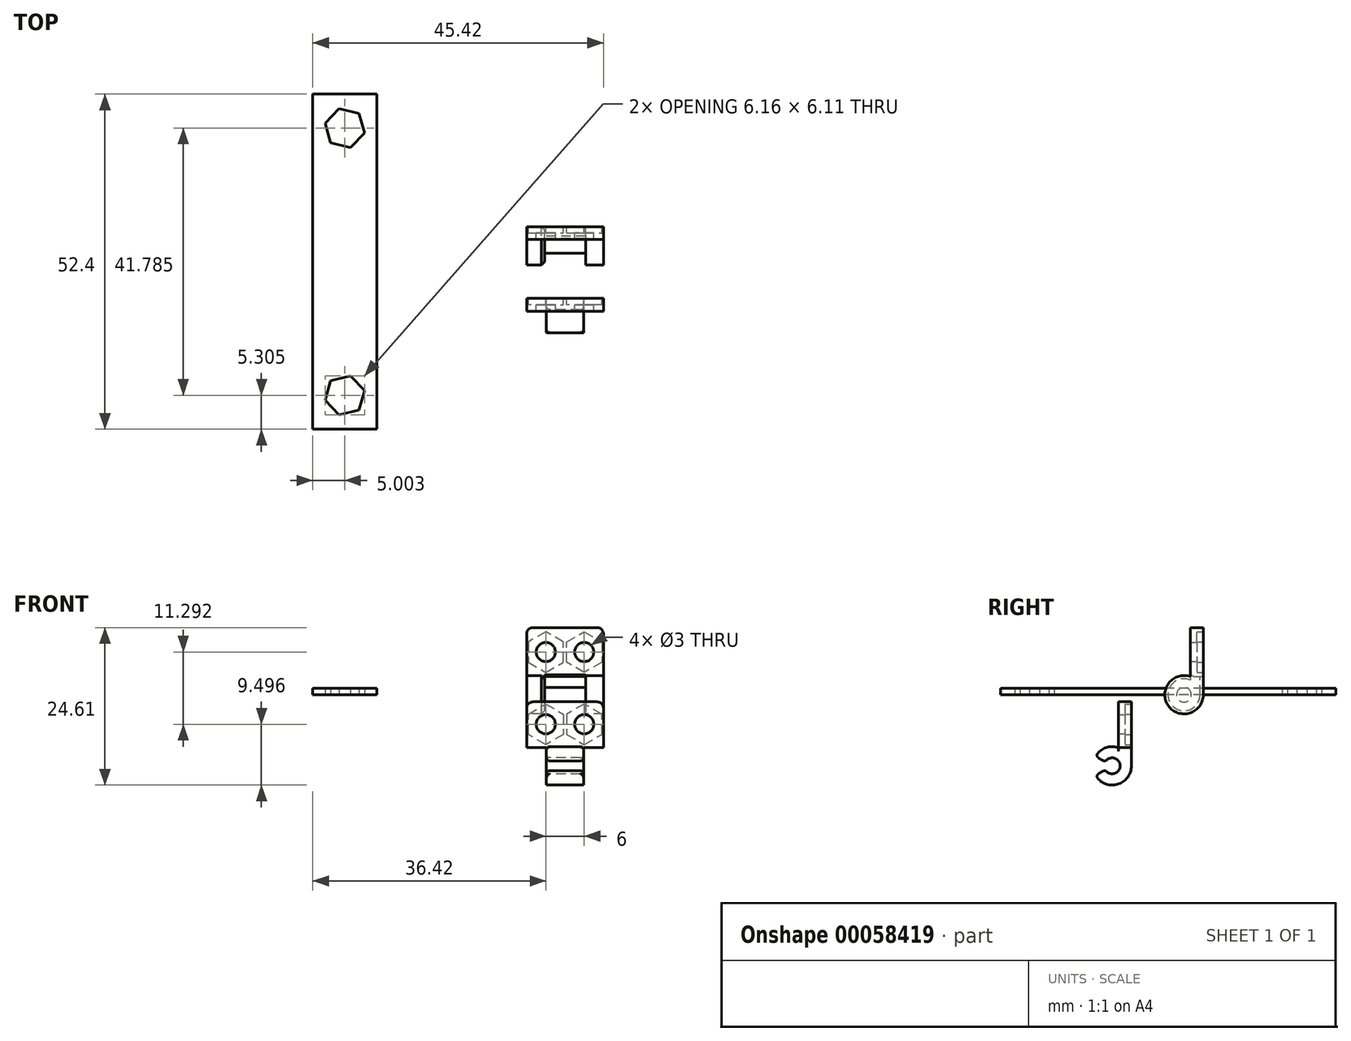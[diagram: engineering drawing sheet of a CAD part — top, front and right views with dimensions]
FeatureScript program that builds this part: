
annotation { "Feature Type Name" : "Feature", "Feature Type Description" : "" }
export const myFeature = defineFeature(function(context is Context, id is Id, definition is map)
    precondition{}
    {
        {
            var Q0;
            Q0=qCreatedBy(makeId("Right.planeOp"),FACE);
            var sketch = newSketch(context, id + "F0", { "sketchPlane" : qUnion([Q0])});
            skCircle(sketch, "E0", {"center": v(-1, 0) * mm, "radius": 3 * mm});
            skLineSegment(sketch, "E1", {"start": v(2, 0) * mm, "end": v(2, 10.5) * mm});
            skLineSegment(sketch, "E2", {"start": v(2, 10.5) * mm, "end": v(0, 10.5) * mm});
            skLineSegment(sketch, "E3", {"start": v(0, 10.5) * mm, "end": v(0, 2.83) * mm});
            skCircle(sketch, "E4", {"center": v(-1, 0) * mm, "radius": 1.15 * mm});
            skLineSegment(sketch, "E5", {"start": v(0, 2.83) * mm, "end": v(2, 2.83) * mm});
            skLineSegment(sketch, "E6", {"start": v(-1, 0) * mm, "end": v(2, 0) * mm, "construction": true});
            skSolve(sketch);
        }
        {
            var Q0;
            Q0=qSketchRegion(id+"F0",true);
            var Q1;
            Q1=makeQuery(id+"F0.imprint","IMPRINT",FACE,{"disambiguationData":[TD([[makeQuery(id+"F0.imprint","IMPRINT",EDGE,{"derivedFrom":sQuery(id+"F0.wireOp",EDGE,"E4")}),1.0]])]});
            var Q2;
            Q2=qBodyType(qCreatedBy(id+"FAZ1pR2O8vTgytI_1",FACE),BodyType.SOLID);
            extrude(context, id + "F1", {"entities" : qUnion([Q0, Q1]), "endBoundEntityFace" : qUnion([Q2]), "depth" : 6 * mm, "hasSecondDirection" : true, "secondDirectionOppositeDirection" : true, "secondDirectionDepth" : 6 * mm});
        }
        {
            var Q0;
            Q0=makeQuery(id+"F0.imprint","IMPRINT",FACE,{"disambiguationData":[TD([[makeQuery(id+"F0.imprint","IMPRINT",EDGE,{"derivedFrom":sQuery(id+"F0.wireOp",EDGE,"E4")}),-1.0]])]});
            var Q1;
            {var subQ0=sQuery(id+"F0.wireOp",EDGE,"E5");Q1=makeQuery(id+"F0.imprint","IMPRINT",FACE,{"disambiguationData":[TD([[makeQuery(id+"F0.imprint","IMPRINT",EDGE,{"derivedFrom":subQ0}),-1.0]])]});}
            extrude(context, id + "F2", {"entities" : qUnion([Q0, Q1]), "operationType" : NewBodyOperationType.REMOVE, "depth" : 3.2 * mm, "hasSecondDirection" : true, "secondDirectionOppositeDirection" : true, "secondDirectionDepth" : 3.2 * mm});
        }
        {
            var Q0;
            Q0=makeQuery(id+"F1.opExtrude","SWEPT_FACE",FACE,{"disambiguationData":[OSD([sQuery(id+"F0.wireOp",EDGE,"E1")])]});
            var sketch = newSketch(context, id + "F3", { "sketchPlane" : qUnion([Q0])});
            skLineSegment(sketch, "E7", {"start": v(-6, 6.68) * mm, "end": v(6, 6.68) * mm, "construction": true});
            skLineSegment(sketch, "E8", {"start": v(0, 10.5) * mm, "end": v(0, 2.83) * mm, "construction": true});
            skCircle(sketch, "E9.cCircle", {"center": v(3, 6.68) * mm, "radius": 2.75 * mm, "construction": true});
            skLineSegment(sketch, "E9.0", {"start": v(3, 3.5) * mm, "end": v(0.25, 5.1) * mm});
            skLineSegment(sketch, "E9.1", {"start": v(0.25, 5.1) * mm, "end": v(0.25, 8.27) * mm});
            skLineSegment(sketch, "E9.2", {"start": v(0.25, 8.27) * mm, "end": v(3, 9.85) * mm});
            skLineSegment(sketch, "E9.3", {"start": v(3, 9.85) * mm, "end": v(5.75, 8.27) * mm});
            skLineSegment(sketch, "E9.4", {"start": v(5.75, 8.27) * mm, "end": v(5.75, 5.1) * mm});
            skLineSegment(sketch, "E9.5", {"start": v(5.75, 5.1) * mm, "end": v(3, 3.5) * mm});
            skPoint(sketch, "E9.0.midPoint", {"position": v(1.63, 4.3) * mm});
            skLineSegment(sketch, "E10", {"start": v(3, 9.85) * mm, "end": v(3, 3.5) * mm, "construction": true});
            skLineSegment(sketch, "E11.MirrorCS", {"start": v(-3, 9.85) * mm, "end": v(-5.75, 8.27) * mm});
            skLineSegment(sketch, "E12.MirrorCS", {"start": v(-0.25, 8.27) * mm, "end": v(-3, 9.85) * mm});
            skLineSegment(sketch, "E13.MirrorCS", {"start": v(-0.25, 5.1) * mm, "end": v(-0.25, 8.27) * mm});
            skLineSegment(sketch, "E14.MirrorCS", {"start": v(-3, 3.5) * mm, "end": v(-0.25, 5.1) * mm});
            skLineSegment(sketch, "E15.MirrorCS", {"start": v(-5.75, 5.1) * mm, "end": v(-3, 3.5) * mm});
            skLineSegment(sketch, "E16.MirrorCS", {"start": v(-5.75, 8.27) * mm, "end": v(-5.75, 5.1) * mm});
            skLineSegment(sketch, "E17", {"start": v(-3, 9.85) * mm, "end": v(-3, 3.5) * mm, "construction": true});
            skPoint(sketch, "E18", {"position": v(-3, 6.68) * mm});
            skSolve(sketch);
        }
        {
            var Q0;
            Q0=makeQuery(id+"F3.imprint","IMPRINT",FACE,{"disambiguationData":[TD([[makeQuery(id+"F3.imprint","IMPRINT",EDGE,{"derivedFrom":sQuery(id+"F3.wireOp",EDGE,"E9.0")}),-1.0]])]});
            var Q1;
            Q1=makeQuery(id+"F3.imprint","IMPRINT",FACE,{"disambiguationData":[TD([[makeQuery(id+"F3.imprint","IMPRINT",EDGE,{"derivedFrom":sQuery(id+"F3.wireOp",EDGE,"E11.MirrorCS")}),1.0]])]});
            var Q2;
            {var subQ9=sQuery(id+"F3.wireOp",EDGE,"E9.1");Q2=makeQuery(id+"F3.imprint","IMPRINT",FACE,{"disambiguationData":[TD([[makeQuery(id+"F3.imprint","IMPRINT",EDGE,{"derivedFrom":subQ9}),-1.0]])]});}
            extrude(context, id + "F4", {"entities" : qUnion([Q0, Q1, Q2]), "operationType" : NewBodyOperationType.REMOVE, "oppositeDirection" : true, "depth" : 1 * mm});
        }
        {
            var Q0;
            Q0=sQuery(id+"F3.wireOp",VERTEX,"E9.cCircle.center");
            var Q1;
            Q1=sQuery(id+"F3.wireOp",VERTEX,"E18");
            var Q2;
            Q2=makeQuery(id+"F1.opExtrude","SWEPT_BODY",BODY,{"disambiguationData":[OSD([sQuery(id+"F0.wireOp",EDGE,"E0"),sQuery(id+"F0.wireOp",EDGE,"E1"),sQuery(id+"F0.wireOp",EDGE,"E2"),sQuery(id+"F0.wireOp",EDGE,"E3")])]});
            hole(context, id + "F5", {"style" : HoleStyle.SIMPLE, "holeDiameter" : 3 * mm, "endStyle" : HoleEndStyle.THROUGH, "locations" : qUnion([Q0, Q1]), "scope" : qUnion([Q2])});
        }
        {
            var Q0;
            Q0=qCreatedBy(makeId("Right.planeOp"),FACE);
            var sketch = newSketch(context, id + "F6", { "sketchPlane" : qUnion([Q0])});
            skCircle(sketch, "E19", {"center": v(-12.22, -11.11) * mm, "radius": 3 * mm});
            skLineSegment(sketch, "E20", {"start": v(-9.22, -11.11) * mm, "end": v(-9.22, -1.11) * mm});
            skLineSegment(sketch, "E21", {"start": v(-9.22, -1.11) * mm, "end": v(-11.22, -1.11) * mm});
            skLineSegment(sketch, "E22", {"start": v(-11.22, -1.11) * mm, "end": v(-11.22, -8.29) * mm});
            skLineSegment(sketch, "E23", {"start": v(-9.22, -11.11) * mm, "end": v(-12.22, -11.11) * mm, "construction": true});
            skCircle(sketch, "E24", {"center": v(-12.22, -11.11) * mm, "radius": 1.25 * mm});
            skLineSegment(sketch, "E25", {"start": v(-12.22, -11.11) * mm, "end": v(-14.82, -9.61) * mm});
            skLineSegment(sketch, "E26", {"start": v(-12.22, -11.11) * mm, "end": v(-14.82, -12.61) * mm});
            skLineSegment(sketch, "E27", {"start": v(-11.22, -8.29) * mm, "end": v(-9.22, -8.29) * mm});
            skSolve(sketch);
        }
        {
            var Q0;
            {var subQ1=sQuery(id+"F6.wireOp",EDGE,"E20");Q0=makeQuery(id+"F6.imprint","IMPRINT",FACE,{"disambiguationData":[TD([[makeQuery(id+"F6.imprint","IMPRINT",EDGE,{"derivedFrom":subQ1}),1.0]])]});}
            var Q1;
            {var subQ3=sQuery(id+"F6.wireOp",EDGE,"E19");var subQ9=makeQuery(id+"F6.imprint","INTERSECT",VERTEX,{"derivedFrom":[subQ3,sQuery(id+"F6.wireOp",EDGE,"E20")]});Q1=makeQuery(id+"F6.imprint","IMPRINT",FACE,{"disambiguationData":[TD([[makeQuery(id+"F6.imprint","IMPRINT",EDGE,{"disambiguationData":[TD([[subQ9,-1.0]])],"derivedFrom":subQ3}),1.0]])]});}
            extrude(context, id + "F7", {"entities" : qUnion([Q0, Q1]), "depth" : 2.9 * mm, "hasSecondDirection" : true, "secondDirectionOppositeDirection" : true, "secondDirectionDepth" : 2.9 * mm});
        }
        {
            var Q0;
            {var subQ1=sQuery(id+"F6.wireOp",EDGE,"E21");Q0=makeQuery(id+"F6.imprint","IMPRINT",FACE,{"disambiguationData":[TD([[makeQuery(id+"F6.imprint","IMPRINT",EDGE,{"derivedFrom":subQ1}),1.0]])]});}
            extrude(context, id + "F8", {"entities" : qUnion([Q0]), "operationType" : NewBodyOperationType.ADD, "endBound" : BoundingType.SYMMETRIC, "depth" : 12 * mm});
        }
        {
            var Q0;
            Q0=makeQuery(id+"F7.opExtrude","SWEPT_EDGE",EDGE,{"disambiguationData":[OSD([sQuery(id+"F6.wireOp",EDGE,"E24"),sQuery(id+"F6.wireOp",EDGE,"E25")])]});
            var Q1;
            Q1=makeQuery(id+"F7.opExtrude","SWEPT_EDGE",EDGE,{"disambiguationData":[OSD([sQuery(id+"F6.wireOp",EDGE,"E24"),sQuery(id+"F6.wireOp",EDGE,"E26")])]});
            var Q2;
            Q2=makeQuery(id+"F7.opExtrude","CAP_EDGE",EDGE,{"disambiguationData":[OSD([sQuery(id+"F6.wireOp",EDGE,"E24")])],"isStart":false});
            var Q3;
            Q3=makeQuery(id+"F7.opExtrude","CAP_EDGE",EDGE,{"disambiguationData":[OSD([sQuery(id+"F6.wireOp",EDGE,"E24")])],"isStart":true});
            var Q4;
            Q4=makeQuery(id+"F7.opExtrude","SWEPT_EDGE",EDGE,{"disambiguationData":[OSD([sQuery(id+"F6.wireOp",EDGE,"E19"),sQuery(id+"F6.wireOp",EDGE,"E25")])]});
            var Q5;
            Q5=makeQuery(id+"F7.opExtrude","CAP_EDGE",EDGE,{"disambiguationData":[OSD([sQuery(id+"F6.wireOp",EDGE,"E26")])],"isStart":false});
            var Q6;
            Q6=makeQuery(id+"F7.opExtrude","SWEPT_EDGE",EDGE,{"disambiguationData":[OSD([sQuery(id+"F6.wireOp",EDGE,"E19"),sQuery(id+"F6.wireOp",EDGE,"E26")])]});
            var Q7;
            Q7=makeQuery(id+"F7.opExtrude","CAP_EDGE",EDGE,{"disambiguationData":[OSD([sQuery(id+"F6.wireOp",EDGE,"E25")])],"isStart":false});
            var Q8;
            Q8=makeQuery(id+"F7.opExtrude","CAP_EDGE",EDGE,{"disambiguationData":[OSD([sQuery(id+"F6.wireOp",EDGE,"E25")])],"isStart":true});
            var Q9;
            Q9=makeQuery(id+"F7.opExtrude","CAP_EDGE",EDGE,{"disambiguationData":[OSD([sQuery(id+"F6.wireOp",EDGE,"E26")])],"isStart":true});
            var Q10;
            {var subQ0=sQuery(id+"F6.wireOp",EDGE,"E19");Q10=makeQuery(id+"F7.opExtrude","CAP_EDGE",EDGE,{"disambiguationData":[OSD([subQ0]),TDD([makeQuery(id+"F6.imprint","IMPRINT",EDGE,{"disambiguationData":[TD([[makeQuery(id+"F6.imprint","INTERSECT",VERTEX,{"derivedFrom":[subQ0,sQuery(id+"F6.wireOp",EDGE,"E22")]}),-1.0]])],"derivedFrom":subQ0})])],"isStart":false});}
            var Q11;
            {var subQ0=sQuery(id+"F6.wireOp",EDGE,"E19");Q11=makeQuery(id+"F7.opExtrude","CAP_EDGE",EDGE,{"disambiguationData":[OSD([subQ0]),TDD([makeQuery(id+"F6.imprint","IMPRINT",EDGE,{"disambiguationData":[TD([[makeQuery(id+"F6.imprint","INTERSECT",VERTEX,{"derivedFrom":[subQ0,sQuery(id+"F6.wireOp",EDGE,"E22")]}),-1.0]])],"derivedFrom":subQ0})])],"isStart":true});}
            var Q12;
            Q12=makeQuery(id+"F7.opExtrude","CAP_EDGE",EDGE,{"disambiguationData":[OSD([sQuery(id+"F6.wireOp",EDGE,"E21")])],"isStart":false});
            var Q13;
            Q13=makeQuery(id+"F7.opExtrude","CAP_EDGE",EDGE,{"disambiguationData":[OSD([sQuery(id+"F6.wireOp",EDGE,"E21")])],"isStart":true});
            fillet(context, id + "F9", {"entities" : qUnion([Q0, Q1, Q2, Q3, Q4, Q5, Q6, Q7, Q8, Q9, Q10, Q11, Q12, Q13]), "radius" : .5 * mm, "tangentPropagation" : true, "allowEdgeOverflow" : false});
        }
        {
            var Q0;
            Q0=makeQuery(id+"F7.opExtrude","SWEPT_FACE",FACE,{"disambiguationData":[OSD([sQuery(id+"F6.wireOp",EDGE,"E20")])]});
            var sketch = newSketch(context, id + "F10", { "sketchPlane" : qUnion([Q0])});
            skCircle(sketch, "E28.cCircle", {"center": v(-3, -4.61) * mm, "radius": 2.75 * mm, "construction": true});
            skLineSegment(sketch, "E28.0", {"start": v(-3, -1.44) * mm, "end": v(-0.25, -3.03) * mm});
            skLineSegment(sketch, "E28.1", {"start": v(-0.25, -3.03) * mm, "end": v(-0.25, -6.2) * mm});
            skLineSegment(sketch, "E28.2", {"start": v(-0.25, -6.2) * mm, "end": v(-3, -7.79) * mm});
            skLineSegment(sketch, "E28.3", {"start": v(-3, -7.79) * mm, "end": v(-5.75, -6.2) * mm});
            skLineSegment(sketch, "E28.4", {"start": v(-5.75, -6.2) * mm, "end": v(-5.75, -3.03) * mm});
            skLineSegment(sketch, "E28.5", {"start": v(-5.75, -3.03) * mm, "end": v(-3, -1.44) * mm});
            skPoint(sketch, "E28.0.midPoint", {"position": v(-1.62, -2.23) * mm});
            skLineSegment(sketch, "E29", {"start": v(-6.92, -4.61) * mm, "end": v(6, -4.61) * mm, "construction": true});
            skLineSegment(sketch, "E30", {"start": v(0, -0.54) * mm, "end": v(0, -9.3) * mm, "construction": true});
            skLineSegment(sketch, "E31.MirrorCS", {"start": v(0.25, -3.03) * mm, "end": v(0.25, -6.2) * mm});
            skLineSegment(sketch, "E32.MirrorCS", {"start": v(3, -1.44) * mm, "end": v(0.25, -3.03) * mm});
            skLineSegment(sketch, "E33.MirrorCS", {"start": v(5.75, -3.03) * mm, "end": v(3, -1.44) * mm});
            skLineSegment(sketch, "E34.MirrorCS", {"start": v(5.75, -6.2) * mm, "end": v(5.75, -3.03) * mm});
            skLineSegment(sketch, "E35.MirrorCS", {"start": v(3, -7.79) * mm, "end": v(5.75, -6.2) * mm});
            skLineSegment(sketch, "E36.MirrorCS", {"start": v(0.25, -6.2) * mm, "end": v(3, -7.79) * mm});
            skPoint(sketch, "E37.MirrorP", {"position": v(3, -4.61) * mm});
            skSolve(sketch);
        }
        {
            var Q0;
            {var subQ13=sQuery(id+"F10.wireOp",EDGE,"E28.0");Q0=makeQuery(id+"F10.imprint","IMPRINT",FACE,{"disambiguationData":[TD([[makeQuery(id+"F10.imprint","IMPRINT",EDGE,{"derivedFrom":subQ13}),-1.0]])]});}
            var Q1;
            Q1=makeQuery(id+"F10.imprint","IMPRINT",FACE,{"disambiguationData":[TD([[makeQuery(id+"F10.imprint","IMPRINT",EDGE,{"derivedFrom":sQuery(id+"F10.wireOp",EDGE,"E31.MirrorCS")}),1.0]])]});
            extrude(context, id + "F11", {"entities" : qUnion([Q0, Q1]), "operationType" : NewBodyOperationType.REMOVE, "oppositeDirection" : true, "depth" : 1 * mm});
        }
        {
            var Q0;
            Q0=sQuery(id+"F10.wireOp",VERTEX,"E28.cCircle.center");
            var Q1;
            Q1=sQuery(id+"F10.wireOp",VERTEX,"E37.MirrorP");
            var Q2;
            Q2=makeQuery(id+"F7.opExtrude","SWEPT_BODY",BODY,{"disambiguationData":[OSD([sQuery(id+"F6.wireOp",EDGE,"E19"),sQuery(id+"F6.wireOp",EDGE,"E20"),sQuery(id+"F6.wireOp",EDGE,"E21"),sQuery(id+"F6.wireOp",EDGE,"E22"),sQuery(id+"F6.wireOp",EDGE,"E24"),sQuery(id+"F6.wireOp",EDGE,"E25"),sQuery(id+"F6.wireOp",EDGE,"E26")])]});
            hole(context, id + "F12", {"style" : HoleStyle.SIMPLE, "holeDiameter" : 3 * mm, "endStyle" : HoleEndStyle.THROUGH, "locations" : qUnion([Q0, Q1]), "scope" : qUnion([Q2])});
        }
        {
            var Q0;
            Q0=makeQuery(id+"F2.boolean.opBoolean","COPY",EDGE,{"derivedFrom":makeQuery(id+"F2.opExtrude","CAP_EDGE",EDGE,{"disambiguationData":[OSD([sQuery(id+"F0.wireOp",EDGE,"E0")])],"isStart":true})});
            var Q1;
            Q1=makeQuery(id+"F2.boolean.opBoolean","COPY",EDGE,{"derivedFrom":makeQuery(id+"F2.opExtrude","CAP_EDGE",EDGE,{"disambiguationData":[OSD([sQuery(id+"F0.wireOp",EDGE,"E0")])],"isStart":false})});
            chamfer(context, id + "F13", {"entities" : qUnion([Q0, Q1]), "width" : .5 * mm, "tangentPropagation" : true});
        }
        {
            var Q0;
            {var subQ0=sQuery(id+"F0.wireOp",EDGE,"E0");var subQ1=sQuery(id+"F0.wireOp",EDGE,"E3");var subQ2=sQuery(id+"F0.wireOp",EDGE,"E5");Q0=makeQuery(id+"F2.boolean.opBoolean","MERGE",EDGE,{"derivedFrom":[makeQuery(id+"F1.opExtrude","SWEPT_EDGE",EDGE,{"disambiguationData":[OSD([subQ0,subQ1,subQ2])]}),makeQuery(id+"F2.opExtrude","SWEPT_EDGE",EDGE,{"disambiguationData":[OSD([subQ0,subQ1,subQ2])]})]});}
            chamfer(context, id + "F14", {"entities" : qUnion([Q0]), "chamferType" : ChamferType.OFFSET_ANGLE, "width" : 0.5 * mm, "oppositeDirection" : false, "angle" : 30 * degree, "tangentPropagation" : true});
        }
        {
            var Q0;
            Q0=qCreatedBy(makeId("Top.planeOp"),FACE);
            var sketch = newSketch(context, id + "F15", { "sketchPlane" : qUnion([Q0])});
            skLineSegment(sketch, "E38.bottom", {"start": v(-39.42, 22.73) * mm, "end": v(-29.42, 22.73) * mm});
            skLineSegment(sketch, "E38.top", {"start": v(-39.42, -29.67) * mm, "end": v(-29.42, -29.67) * mm});
            skLineSegment(sketch, "E38.left", {"start": v(-39.42, 22.73) * mm, "end": v(-39.42, -29.67) * mm});
            skLineSegment(sketch, "E38.right", {"start": v(-29.42, 22.73) * mm, "end": v(-29.42, -29.67) * mm});
            skCircle(sketch, "E39.cCircle", {"center": v(-34.42, 17.42) * mm, "radius": 2.75 * mm, "construction": true});
            skLineSegment(sketch, "E39.0", {"start": v(-33.54, 14.37) * mm, "end": v(-36.62, 15.14) * mm});
            skLineSegment(sketch, "E39.1", {"start": v(-36.62, 15.14) * mm, "end": v(-37.5, 18.2) * mm});
            skLineSegment(sketch, "E39.2", {"start": v(-37.5, 18.2) * mm, "end": v(-35.3, 20.47) * mm});
            skLineSegment(sketch, "E39.3", {"start": v(-35.3, 20.47) * mm, "end": v(-32.21, 19.7) * mm});
            skLineSegment(sketch, "E39.4", {"start": v(-32.21, 19.7) * mm, "end": v(-31.34, 16.65) * mm});
            skLineSegment(sketch, "E39.5", {"start": v(-31.34, 16.65) * mm, "end": v(-33.54, 14.37) * mm});
            skPoint(sketch, "E39.0.midPoint", {"position": v(-35.08, 14.75) * mm});
            skLineSegment(sketch, "E40", {"start": v(-39.42, -3.47) * mm, "end": v(-29.42, -3.47) * mm, "construction": true});
            skLineSegment(sketch, "E41.MirrorCS", {"start": v(-31.34, -23.6) * mm, "end": v(-33.54, -21.31) * mm});
            skLineSegment(sketch, "E42.MirrorCS", {"start": v(-32.21, -26.65) * mm, "end": v(-31.34, -23.6) * mm});
            skLineSegment(sketch, "E43.MirrorCS", {"start": v(-35.3, -27.42) * mm, "end": v(-32.21, -26.65) * mm});
            skLineSegment(sketch, "E44.MirrorCS", {"start": v(-37.5, -25.13) * mm, "end": v(-35.3, -27.42) * mm});
            skLineSegment(sketch, "E45.MirrorCS", {"start": v(-36.62, -22.08) * mm, "end": v(-37.5, -25.13) * mm});
            skLineSegment(sketch, "E46.MirrorCS", {"start": v(-33.54, -21.31) * mm, "end": v(-36.62, -22.08) * mm});
            skSolve(sketch);
        }
        {
            var Q0;
            Q0=makeQuery(id+"F15.imprint","IMPRINT",FACE,{"disambiguationData":[TD([[makeQuery(id+"F15.imprint","IMPRINT",EDGE,{"derivedFrom":sQuery(id+"F15.wireOp",EDGE,"E38.bottom")}),-1.0]])]});
            extrude(context, id + "F16", {"entities" : qUnion([Q0]), "depth" : 1 * mm});
        }
        {
            var Q0;
            Q0=qCreatedBy(makeId("Top.planeOp"),FACE);
            var sketch = newSketch(context, id + "F17", { "sketchPlane" : qUnion([Q0])});
            skLineSegment(sketch, "E47.bottom", {"start": v(0, -14.87) * mm, "end": v(13.7, -14.87) * mm});
            skLineSegment(sketch, "E47.top", {"start": v(0, -16.64) * mm, "end": v(13.7, -16.64) * mm});
            skLineSegment(sketch, "E47.left", {"start": v(0, -14.87) * mm, "end": v(0, -16.64) * mm});
            skLineSegment(sketch, "E47.right", {"start": v(13.7, -14.87) * mm, "end": v(13.7, -16.64) * mm});
            skSolve(sketch);
        }
        {
            var Q0;
            Q0=qCreatedBy(makeId("Top.planeOp"),FACE);
            cPlane(context, id + "F18", {"entities" : qUnion([Q0]), "cplaneType" : CPlaneType.OFFSET, "offset" : 50 * mm, "width" : 150 * mm, "height" : 150 * mm});
        }
        {
            var Q0;
            Q0=qCreatedBy(id+"F18.planeOp",FACE);
            var sketch = newSketch(context, id + "F19", { "sketchPlane" : qUnion([Q0])});
            skLineSegment(sketch, "E48.bottom", {"start": v(0, -13.35) * mm, "end": v(14.66, -13.35) * mm});
            skLineSegment(sketch, "E48.top", {"start": v(0, -15.86) * mm, "end": v(14.66, -15.86) * mm});
            skLineSegment(sketch, "E48.left", {"start": v(0, -13.35) * mm, "end": v(0, -15.86) * mm});
            skLineSegment(sketch, "E48.right", {"start": v(14.66, -13.35) * mm, "end": v(14.66, -15.86) * mm});
            skSolve(sketch);
        }
        {
            var Q0;
            Q0=makeQuery(id+"F1.opExtrude","CAP_EDGE",EDGE,{"disambiguationData":[OSD([sQuery(id+"F0.wireOp",EDGE,"E2")])],"isStart":true});
            var Q1;
            Q1=makeQuery(id+"F1.opExtrude","CAP_EDGE",EDGE,{"disambiguationData":[OSD([sQuery(id+"F0.wireOp",EDGE,"E2")])],"isStart":false});
            var Q2;
            Q2=makeQuery(id+"F8.opExtrude","CAP_EDGE",EDGE,{"disambiguationData":[OSD([sQuery(id+"F6.wireOp",EDGE,"E21")])],"isStart":false});
            var Q3;
            Q3=makeQuery(id+"F8.opExtrude","CAP_EDGE",EDGE,{"disambiguationData":[OSD([sQuery(id+"F6.wireOp",EDGE,"E21")])],"isStart":true});
            fillet(context, id + "F20", {"entities" : qUnion([Q0, Q1, Q2, Q3]), "radius" : 1 * mm, "tangentPropagation" : true, "allowEdgeOverflow" : false});
        }
    });
